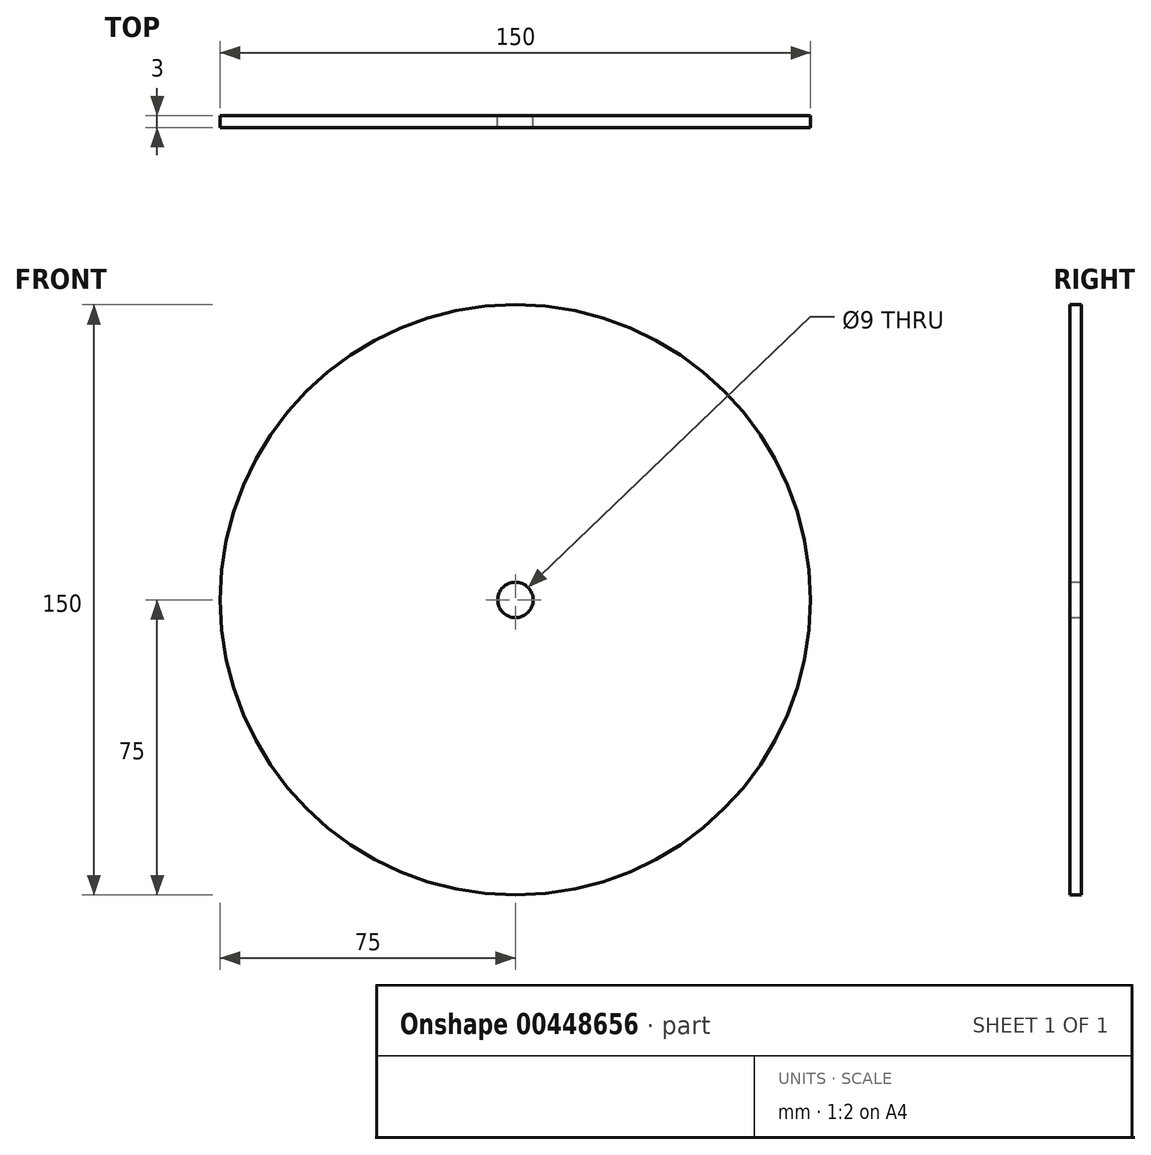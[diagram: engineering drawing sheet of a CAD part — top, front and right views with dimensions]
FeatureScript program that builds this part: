
annotation { "Feature Type Name" : "Feature", "Feature Type Description" : "" }
export const myFeature = defineFeature(function(context is Context, id is Id, definition is map)
    precondition{}
    {
        {
            var Q0;
            Q0=qCreatedBy(makeId("Front.planeOp"),FACE);
            var sketch = newSketch(context, id + "F0", { "sketchPlane" : qUnion([Q0])});
            skCircle(sketch, "E0", {"center": v(0, 0) * mm, "radius": 75 * mm});
            skCircle(sketch, "E1", {"center": v(0, 0) * mm, "radius": 4.5 * mm});
            skSolve(sketch);
        }
        {
            var Q0;
            Q0=makeQuery(id+"F0.imprint","IMPRINT",FACE,{"disambiguationData":[TD([[makeQuery(id+"F0.imprint","IMPRINT",EDGE,{"derivedFrom":sQuery(id+"F0.wireOp",EDGE,"E0")}),1.0]])]});
            extrude(context, id + "F1", {"entities" : qUnion([Q0]), "depth" : 3 * mm});
        }
    });
